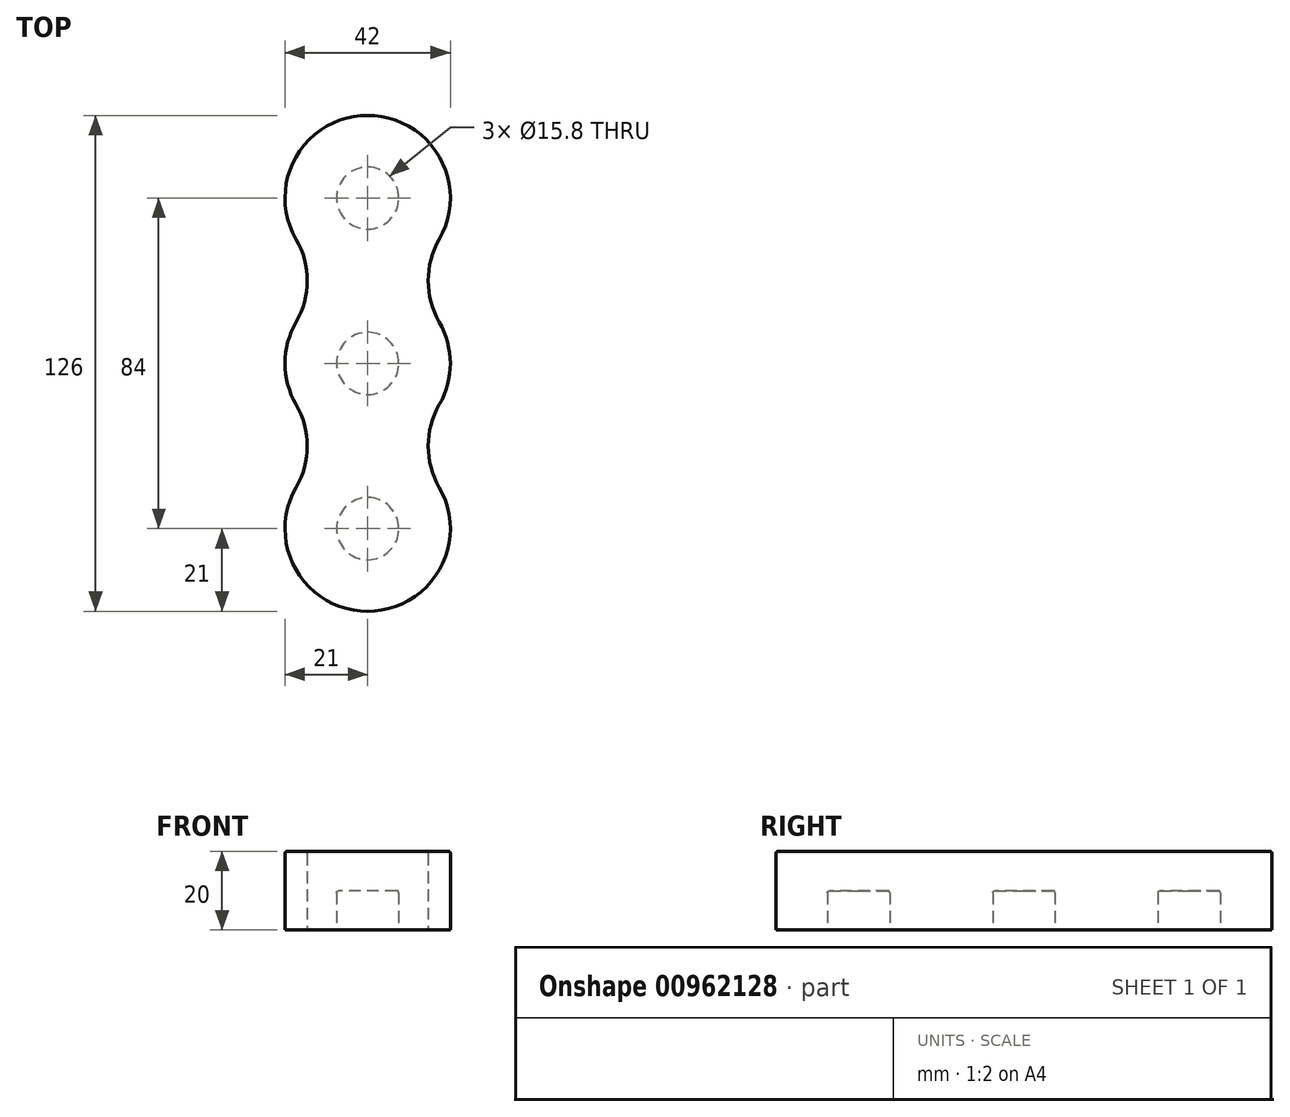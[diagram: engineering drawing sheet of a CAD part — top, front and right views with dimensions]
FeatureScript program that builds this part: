
annotation { "Feature Type Name" : "Feature", "Feature Type Description" : "" }
export const myFeature = defineFeature(function(context is Context, id is Id, definition is map)
    precondition{}
    {
        {
            assignVariable(context, id + "F0", {"name" : "inner_circle_extrude", "anyValue" : 10});
        }
        {
            assignVariable(context, id + "F1", {"name" : "outer_circle_extrude", "anyValue" : 20});
        }
        {
            assignVariable(context, id + "F2", {"name" : "fillet", "anyValue" : 0.5});
        }
        {
            var Q0;
            Q0=qCreatedBy(makeId("Top.planeOp"),FACE);
            var sketch = newSketch(context, id + "F3", { "sketchPlane" : qUnion([Q0])});
            skCircle(sketch, "E0", {"center": v(0, 42) * mm, "radius": 7.9 * mm});
            skCircle(sketch, "E1", {"center": v(0, 0) * mm, "radius": 7.9 * mm});
            skArc(sketch, "E2.converted", {"start": v(18.19, 31.5) * mm, "mid": v(21, 42) * mm, "end": v(18.19, 52.5) * mm});
            skArc(sketch, "E3.converted", {"start": v(-18.19, 10.5) * mm, "mid": v(0, -21) * mm, "end": v(18.19, 10.5) * mm});
            skPoint(sketch, "E4.orphan", {"position": v(-18.87, 9.22) * mm});
            skArc(sketch, "E5", {"start": v(-18.19, 10.5) * mm, "mid": v(-15.37, 21) * mm, "end": v(-18.19, 31.5) * mm});
            skArc(sketch, "E6.MirrorC", {"start": v(18.19, 10.5) * mm, "mid": v(15.37, 21) * mm, "end": v(18.19, 31.5) * mm});
            skArc(sketch, "E7", {"start": v(18.19, 73.5) * mm, "mid": v(0, 105) * mm, "end": v(-18.19, 73.5) * mm});
            skArc(sketch, "E8", {"start": v(-18.19, 52.5) * mm, "mid": v(-15.37, 63) * mm, "end": v(-18.19, 73.5) * mm});
            skArc(sketch, "E9", {"start": v(18.19, 73.5) * mm, "mid": v(15.37, 63) * mm, "end": v(18.19, 52.5) * mm});
            skCircle(sketch, "E10", {"center": v(0, 84) * mm, "radius": 7.9 * mm});
            skArc(sketch, "E11.trimOffspring", {"start": v(-18.19, 52.5) * mm, "mid": v(-21, 42) * mm, "end": v(-18.19, 31.5) * mm});
            skSolve(sketch);
        }
        {
            var Q0;
            Q0=makeQuery(id+"F3.imprint","IMPRINT",FACE,{"disambiguationData":[TD([[makeQuery(id+"F3.imprint","IMPRINT",EDGE,{"derivedFrom":sQuery(id+"F3.wireOp",EDGE,"ScaTM9CG-l0WX-AUfX-dH3G-diZ5i2Zft3Bz")}),1.0]])]});
            var Q1;
            Q1=makeQuery(id+"F3.imprint","IMPRINT",FACE,{"disambiguationData":[TD([[makeQuery(id+"F3.imprint","IMPRINT",EDGE,{"derivedFrom":sQuery(id+"F3.wireOp",EDGE,"E0")}),1.0]])]});
            var Q2;
            Q2=makeQuery(id+"F3.imprint","IMPRINT",FACE,{"disambiguationData":[TD([[makeQuery(id+"F3.imprint","IMPRINT",EDGE,{"derivedFrom":sQuery(id+"F3.wireOp",EDGE,"E1")}),1.0]])]});
            var Q3;
            Q3=makeQuery(id+"F3.imprint","IMPRINT",FACE,{"disambiguationData":[TD([[makeQuery(id+"F3.imprint","IMPRINT",EDGE,{"derivedFrom":sQuery(id+"F3.wireOp",EDGE,"E0")}),-1.0]])]});
            var Q4;
            Q4=makeQuery(id+"F3.imprint","IMPRINT",FACE,{"disambiguationData":[TD([[makeQuery(id+"F3.imprint","IMPRINT",EDGE,{"derivedFrom":sQuery(id+"F3.wireOp",EDGE,"E10")}),1.0]])]});
            extrude(context, id + "F4", {"entities" : qUnion([Q0, Q1, Q2, Q3, Q4]), "depth" : (getVariable(context, 'outer_circle_extrude')) * mm, "offsetDistance" : 25 * mm});
        }
        {
            var Q0;
            Q0=makeQuery(id+"F3.imprint","IMPRINT",FACE,{"disambiguationData":[TD([[makeQuery(id+"F3.imprint","IMPRINT",EDGE,{"derivedFrom":sQuery(id+"F3.wireOp",EDGE,"E0")}),1.0]])]});
            var Q1;
            Q1=makeQuery(id+"F3.imprint","IMPRINT",FACE,{"disambiguationData":[TD([[makeQuery(id+"F3.imprint","IMPRINT",EDGE,{"derivedFrom":sQuery(id+"F3.wireOp",EDGE,"E1")}),1.0]])]});
            var Q2;
            Q2=makeQuery(id+"F3.imprint","IMPRINT",FACE,{"disambiguationData":[TD([[makeQuery(id+"F3.imprint","IMPRINT",EDGE,{"derivedFrom":sQuery(id+"F3.wireOp",EDGE,"E10")}),1.0]])]});
            extrude(context, id + "F5", {"entities" : qUnion([Q0, Q1, Q2]), "operationType" : NewBodyOperationType.REMOVE, "depth" : (getVariable(context, 'inner_circle_extrude')) * mm, "offsetDistance" : 25 * mm});
        }
        {
            var Q0;
            Q0=makeQuery(id+"Fh60y82bb3ZeJ6P_1.opExtrude","CAP_EDGE",EDGE,{"disambiguationData":[OSD([sQuery(id+"FYH32zqiSheK3IR_1.wireOp",EDGE,"TbaiLBrU-Z3Ny-jN2L-MQj9-D1CM9g1Anb7U")])],"isStart":false});
            var Q1;
            Q1=makeQuery(id+"F4.opExtrude","CAP_EDGE",EDGE,{"disambiguationData":[OSD([sQuery(id+"F3.wireOp",EDGE,"ScaTM9CG-l0WX-AUfX-dH3G-diZ5i2Zft3Bz")])],"isStart":false});
            var Q2;
            Q2=makeQuery(id+"F4.opExtrude","CAP_EDGE",EDGE,{"disambiguationData":[OSD([sQuery(id+"F3.wireOp",EDGE,"ScaTM9CG-l0WX-AUfX-dH3G-diZ5i2Zft3Bz")])],"isStart":true});
            var Q3;
            Q3=makeQuery(id+"F5.boolean.opBoolean","COPY",EDGE,{"derivedFrom":makeQuery(id+"F5.opExtrude","CAP_EDGE",EDGE,{"disambiguationData":[OSD([sQuery(id+"F3.wireOp",EDGE,"E0")])],"isStart":true})});
            var Q4;
            Q4=makeQuery(id+"F5.boolean.opBoolean","COPY",FACE,{"derivedFrom":makeQuery(id+"F5.opExtrude","CAP_FACE",FACE,{"disambiguationData":[OSD([sQuery(id+"F3.wireOp",EDGE,"E0")])],"isStart":false})});
            var Q5;
            Q5=makeQuery(id+"F5.boolean.opBoolean","COPY",EDGE,{"derivedFrom":makeQuery(id+"F5.opExtrude","CAP_EDGE",EDGE,{"disambiguationData":[OSD([sQuery(id+"F3.wireOp",EDGE,"E1")])],"isStart":true})});
            var Q6;
            Q6=makeQuery(id+"F5.boolean.opBoolean","COPY",EDGE,{"derivedFrom":makeQuery(id+"F5.opExtrude","CAP_EDGE",EDGE,{"disambiguationData":[OSD([sQuery(id+"F3.wireOp",EDGE,"E1")])],"isStart":false})});
            var Q7;
            Q7=makeQuery(id+"Fh60y82bb3ZeJ6P_1.opExtrude","CAP_EDGE",EDGE,{"disambiguationData":[OSD([sQuery(id+"FYH32zqiSheK3IR_1.wireOp",EDGE,"Dg55u7MG-Wcnn-qXMQ-j3jR-78wnB7IFwmOc")])],"isStart":true});
            var Q8;
            Q8=makeQuery(id+"Fh60y82bb3ZeJ6P_1.opExtrude","CAP_EDGE",EDGE,{"disambiguationData":[OSD([sQuery(id+"FYH32zqiSheK3IR_1.wireOp",EDGE,"Dg55u7MG-Wcnn-qXMQ-j3jR-78wnB7IFwmOc")])],"isStart":false});
            var Q9;
            Q9=makeQuery(id+"Fh60y82bb3ZeJ6P_1.opExtrude","CAP_EDGE",EDGE,{"disambiguationData":[OSD([sQuery(id+"FYH32zqiSheK3IR_1.wireOp",EDGE,"yYbwziLd-AT4g-cY9H-HqPF-seHZ7fr9480S")])],"isStart":false});
            var Q10;
            Q10=makeQuery(id+"Fh60y82bb3ZeJ6P_1.opExtrude","CAP_EDGE",EDGE,{"disambiguationData":[OSD([sQuery(id+"FYH32zqiSheK3IR_1.wireOp",EDGE,"yYbwziLd-AT4g-cY9H-HqPF-seHZ7fr9480S")])],"isStart":true});
            var Q11;
            Q11=makeQuery(id+"F4.opExtrude","CAP_EDGE",EDGE,{"disambiguationData":[OSD([sQuery(id+"F3.wireOp",EDGE,"E2.converted")])],"isStart":false});
            var Q12;
            Q12=makeQuery(id+"Fh60y82bb3ZeJ6P_1.opExtrude","CAP_EDGE",EDGE,{"disambiguationData":[OSD([sQuery(id+"FYH32zqiSheK3IR_1.wireOp",EDGE,"wx7rLj1W-yxu7-wHSL-2GXC-TRnYSJiHQu1A")])],"isStart":false});
            var Q13;
            Q13=makeQuery(id+"Fh60y82bb3ZeJ6P_1.opExtrude","CAP_EDGE",EDGE,{"disambiguationData":[OSD([sQuery(id+"FYH32zqiSheK3IR_1.wireOp",EDGE,"wx7rLj1W-yxu7-wHSL-2GXC-TRnYSJiHQu1A")])],"isStart":true});
            var Q14;
            Q14=makeQuery(id+"F5.boolean.opBoolean","COPY",EDGE,{"derivedFrom":makeQuery(id+"F5.opExtrude","CAP_EDGE",EDGE,{"disambiguationData":[OSD([sQuery(id+"F3.wireOp",EDGE,"E10")])],"isStart":false})});
            var Q15;
            Q15=makeQuery(id+"F5.boolean.opBoolean","COPY",EDGE,{"derivedFrom":makeQuery(id+"F5.opExtrude","CAP_EDGE",EDGE,{"disambiguationData":[OSD([sQuery(id+"F3.wireOp",EDGE,"E10")])],"isStart":true})});
            var Q16;
            Q16=makeQuery(id+"Fh60y82bb3ZeJ6P_1.opExtrude","CAP_EDGE",EDGE,{"disambiguationData":[OSD([sQuery(id+"FYH32zqiSheK3IR_1.wireOp",EDGE,"TbaiLBrU-Z3Ny-jN2L-MQj9-D1CM9g1Anb7U")])],"isStart":true});
            fillet(context, id + "F6", {"entities" : qUnion([Q0, Q1, Q2, Q3, Q4, Q5, Q6, Q7, Q8, Q9, Q10, Q11, Q12, Q13, Q14, Q15, Q16]), "radius" : (getVariable(context, 'fillet')) * mm, "tangentPropagation" : true, "allowEdgeOverflow" : false});
        }
    });
